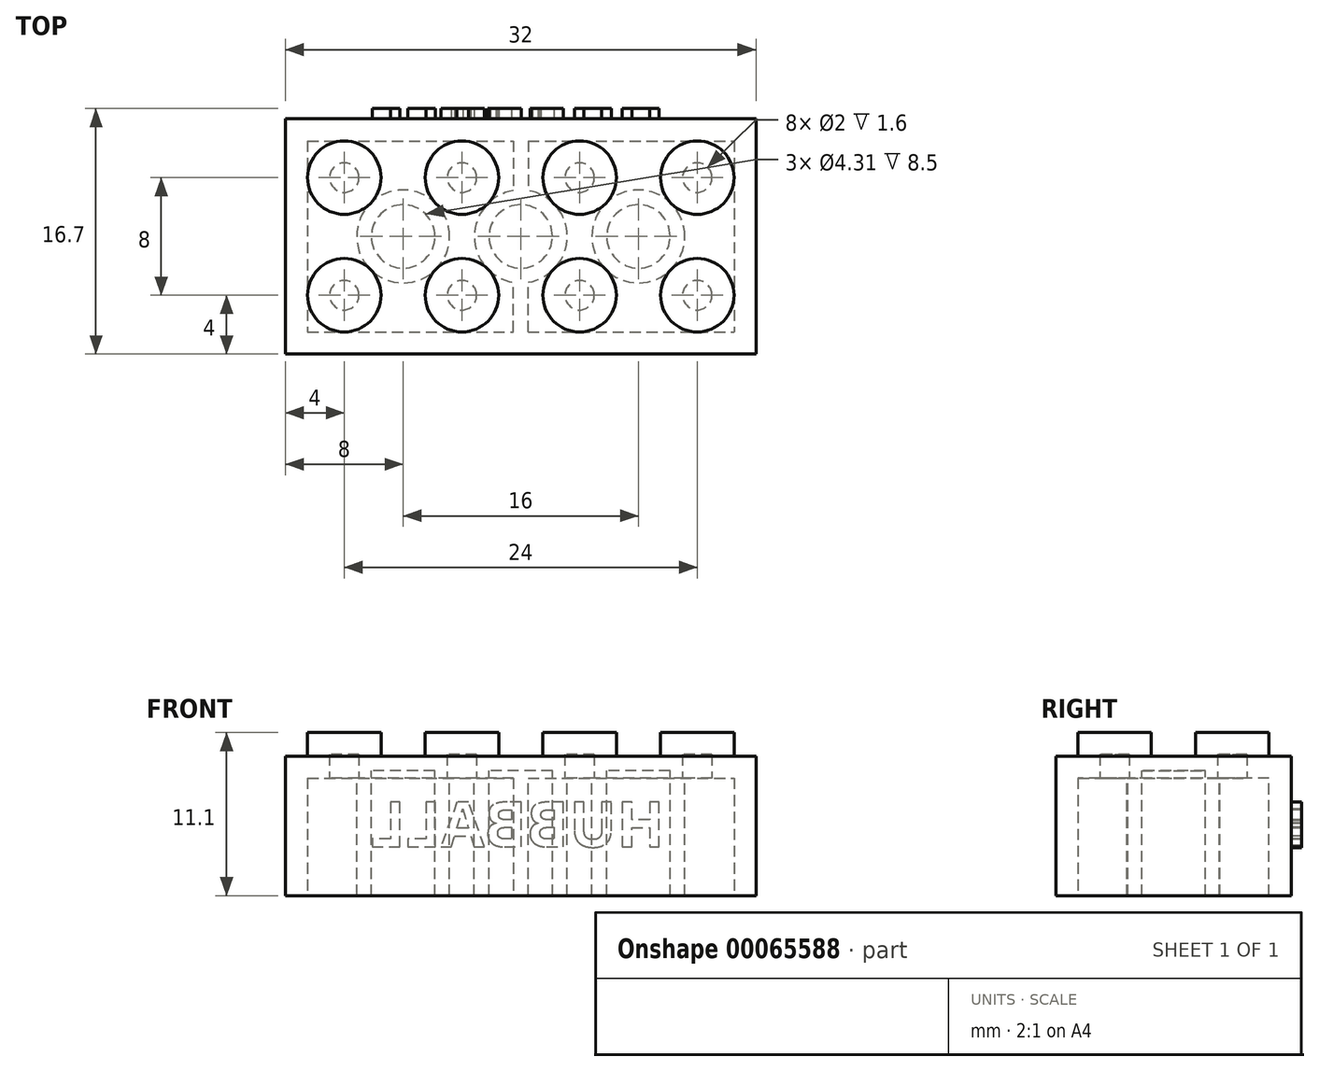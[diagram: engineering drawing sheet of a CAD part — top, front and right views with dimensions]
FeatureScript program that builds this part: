
annotation { "Feature Type Name" : "Feature", "Feature Type Description" : "" }
export const myFeature = defineFeature(function(context is Context, id is Id, definition is map)
    precondition{}
    {
        {
            var Q0;
            Q0=qCreatedBy(makeId("Top.planeOp"),FACE);
            var sketch = newSketch(context, id + "F0", { "sketchPlane" : qUnion([Q0])});
            skLineSegment(sketch, "E0.rect.bottom", {"start": v(-16, 8) * mm, "end": v(16, 8) * mm});
            skLineSegment(sketch, "E0.rect.top", {"start": v(-16, -8) * mm, "end": v(16, -8) * mm});
            skLineSegment(sketch, "E0.rect.left", {"start": v(-16, 8) * mm, "end": v(-16, -8) * mm});
            skLineSegment(sketch, "E0.rect.right", {"start": v(16, 8) * mm, "end": v(16, -8) * mm});
            skPoint(sketch, "E0.rect.middle", {"position": v(0, 0) * mm});
            skSolve(sketch);
        }
        {
            var Q0;
            Q0=makeQuery(id+"F0.imprint","IMPRINT",FACE,{"disambiguationData":[TD([[makeQuery(id+"F0.imprint","IMPRINT",EDGE,{"derivedFrom":sQuery(id+"F0.wireOp",EDGE,"E0.rect.bottom")}),-1.0]])]});
            extrude(context, id + "F1", {"entities" : qUnion([Q0]), "depth" : 9.5 * mm});
        }
        {
            var Q0;
            Q0=makeQuery(id+"F1.opExtrude","CAP_FACE",FACE,{"disambiguationData":[OSD([sQuery(id+"F0.wireOp",EDGE,"E0.rect.bottom"),sQuery(id+"F0.wireOp",EDGE,"E0.rect.top"),sQuery(id+"F0.wireOp",EDGE,"E0.rect.left"),sQuery(id+"F0.wireOp",EDGE,"E0.rect.right")])],"isStart":false});
            var sketch = newSketch(context, id + "F2", { "sketchPlane" : qUnion([Q0])});
            skPoint(sketch, "E1.rect.middle", {"position": v(-8, 0) * mm});
            skCircle(sketch, "E2", {"center": v(-12, 4) * mm, "radius": 2.5 * mm});
            skCircle(sketch, "E3", {"center": v(-12, -4) * mm, "radius": 2.5 * mm});
            skCircle(sketch, "E4", {"center": v(-4, 4) * mm, "radius": 2.5 * mm});
            skCircle(sketch, "E5", {"center": v(-4, -4) * mm, "radius": 2.5 * mm});
            skCircle(sketch, "E6.MirrorC", {"center": v(4, 4) * mm, "radius": 2.5 * mm});
            skCircle(sketch, "E7.MirrorC", {"center": v(12, 4) * mm, "radius": 2.5 * mm});
            skCircle(sketch, "E8.MirrorC", {"center": v(12, -4) * mm, "radius": 2.5 * mm});
            skCircle(sketch, "E9.MirrorC", {"center": v(4, -4) * mm, "radius": 2.5 * mm});
            skSolve(sketch);
        }
        {
            var Q0;
            Q0 = qSketchRegion(id + "F2", true);
            extrude(context, id + "F3", {"entities" : qUnion([Q0]), "operationType" : NewBodyOperationType.ADD, "depth" : 1.6 * mm});
        }
        {
            var Q0;
            Q0=makeQuery(id+"F1.opExtrude","CAP_FACE",FACE,{"disambiguationData":[OSD([sQuery(id+"F0.wireOp",EDGE,"E0.rect.bottom"),sQuery(id+"F0.wireOp",EDGE,"E0.rect.top"),sQuery(id+"F0.wireOp",EDGE,"E0.rect.left"),sQuery(id+"F0.wireOp",EDGE,"E0.rect.right")])],"isStart":false});
            var sketch = newSketch(context, id + "F4", { "sketchPlane" : qUnion([Q0])});
            skCircle(sketch, "E10", {"center": v(0, 0) * mm, "radius": 3.16 * mm});
            skLineSegment(sketch, "E11", {"start": v(0, 8) * mm, "end": v(-16, 8) * mm});
            skLineSegment(sketch, "E12", {"start": v(-16, 8) * mm, "end": v(-8, 8) * mm});
            skLineSegment(sketch, "E13", {"start": v(-8, -8) * mm, "end": v(0, -8) * mm});
            skLineSegment(sketch, "E14", {"start": v(0, -8) * mm, "end": v(16, -8) * mm});
            skLineSegment(sketch, "E15", {"start": v(16, -8) * mm, "end": v(8, -8) * mm});
            skLineSegment(sketch, "E16", {"start": v(0, 8) * mm, "end": v(8, 8) * mm});
            skCircle(sketch, "E17.MirrorC", {"center": v(-8, 0) * mm, "radius": 3.16 * mm});
            skCircle(sketch, "E18.MirrorC", {"center": v(8, 0) * mm, "radius": 3.16 * mm});
            skSolve(sketch);
        }
        {
            var Q0;
            Q0=makeQuery(id+"F1.opExtrude","CAP_FACE",FACE,{"disambiguationData":[OSD([sQuery(id+"F0.wireOp",EDGE,"E0.rect.bottom"),sQuery(id+"F0.wireOp",EDGE,"E0.rect.top"),sQuery(id+"F0.wireOp",EDGE,"E0.rect.left"),sQuery(id+"F0.wireOp",EDGE,"E0.rect.right")])],"isStart":true});
            shell(context, id + "F5", {"entities" : qUnion([Q0]), "thickness" : 1.5 * mm});
        }
        {
            var Q0;
            Q0 = qSketchRegion(id + "F4", true);
            extrude(context, id + "F6", {"entities" : qUnion([Q0]), "operationType" : NewBodyOperationType.ADD, "oppositeDirection" : true, "depth" : 9.5 * mm});
        }
        {
            var Q0;
            Q0=makeQuery(id+"F6.opExtrude","CAP_FACE",FACE,{"disambiguationData":[OSD([sQuery(id+"F4.wireOp",EDGE,"E18.MirrorC")])],"isStart":false});
            var Q1;
            Q1=makeQuery(id+"F6.opExtrude","CAP_FACE",FACE,{"disambiguationData":[OSD([sQuery(id+"F4.wireOp",EDGE,"E10")])],"isStart":false});
            var Q2;
            Q2=makeQuery(id+"F6.opExtrude","CAP_FACE",FACE,{"disambiguationData":[OSD([sQuery(id+"F4.wireOp",EDGE,"E17.MirrorC")])],"isStart":false});
            shell(context, id + "F7", {"entities" : qUnion([Q0, Q1, Q2]), "thickness" : 1 * mm});
        }
        {
            var Q0;
            Q0=makeQuery(id+"F1.opExtrude","CAP_FACE",FACE,{"disambiguationData":[OSD([sQuery(id+"F0.wireOp",EDGE,"E0.rect.bottom"),sQuery(id+"F0.wireOp",EDGE,"E0.rect.top"),sQuery(id+"F0.wireOp",EDGE,"E0.rect.left"),sQuery(id+"F0.wireOp",EDGE,"E0.rect.right")])],"isStart":false});
            var sketch = newSketch(context, id + "F8", { "sketchPlane" : qUnion([Q0])});
            skLineSegment(sketch, "E19.bottom", {"start": v(0, 8) * mm, "end": v(0.5, 8) * mm});
            skLineSegment(sketch, "E19.top", {"start": v(0, 3.12) * mm, "end": v(0.5, 3.12) * mm});
            skLineSegment(sketch, "E19.left", {"start": v(0, 8) * mm, "end": v(0, 3.12) * mm});
            skLineSegment(sketch, "E19.right", {"start": v(0.5, 8) * mm, "end": v(0.5, 3.12) * mm});
            skLineSegment(sketch, "E20.MirrorCS", {"start": v(0, 3.12) * mm, "end": v(-0.5, 3.12) * mm});
            skLineSegment(sketch, "E21.MirrorCS", {"start": v(-0.5, 8) * mm, "end": v(-0.5, 3.12) * mm});
            skLineSegment(sketch, "E22.MirrorCS", {"start": v(0, 8) * mm, "end": v(-0.5, 8) * mm});
            skLineSegment(sketch, "E23.MirrorCS", {"start": v(0, -8) * mm, "end": v(-0.5, -8) * mm});
            skLineSegment(sketch, "E24.MirrorCS", {"start": v(0, -8) * mm, "end": v(0.5, -8) * mm});
            skLineSegment(sketch, "E25.MirrorCS", {"start": v(0, -3.12) * mm, "end": v(0.5, -3.12) * mm});
            skLineSegment(sketch, "E26.MirrorCS", {"start": v(0, -3.12) * mm, "end": v(-0.5, -3.12) * mm});
            skLineSegment(sketch, "E27.MirrorCS", {"start": v(-0.5, -8) * mm, "end": v(-0.5, -3.12) * mm});
            skLineSegment(sketch, "E28.MirrorCS", {"start": v(0, -8) * mm, "end": v(0, -3.12) * mm});
            skLineSegment(sketch, "E29.MirrorCS", {"start": v(0.5, -8) * mm, "end": v(0.5, -3.12) * mm});
            skSolve(sketch);
        }
        {
            var Q0;
            Q0 = qSketchRegion(id + "F8", true);
            extrude(context, id + "F9", {"entities" : qUnion([Q0]), "operationType" : NewBodyOperationType.ADD, "oppositeDirection" : true, "depth" : 9.5 * mm});
        }
        {
            var Q0;
            Q0=makeQuery(id+"F1.opExtrude","SWEPT_FACE",FACE,{"disambiguationData":[OSD([sQuery(id+"F0.wireOp",EDGE,"E0.rect.bottom")])]});
            var sketch = newSketch(context, id + "F10", { "sketchPlane" : qUnion([Q0])});
            skText(sketch, "E30", { "text": "HUBBALL", "fontName": "OpenSans-Bold.ttf"});
            const initialGuessF10  = {"E30": [-0.00979, 0.00332, 1, 0, 0.00308]};
            skSetInitialGuess(sketch, initialGuessF10);
            skSolve(sketch);
        }
        {
            var Q0;
            Q0 = qSketchRegion(id + "F10", true);
            extrude(context, id + "F11", {"entities" : qUnion([Q0]), "operationType" : NewBodyOperationType.ADD, "depth" : 0.7 * mm});
        }
    });
